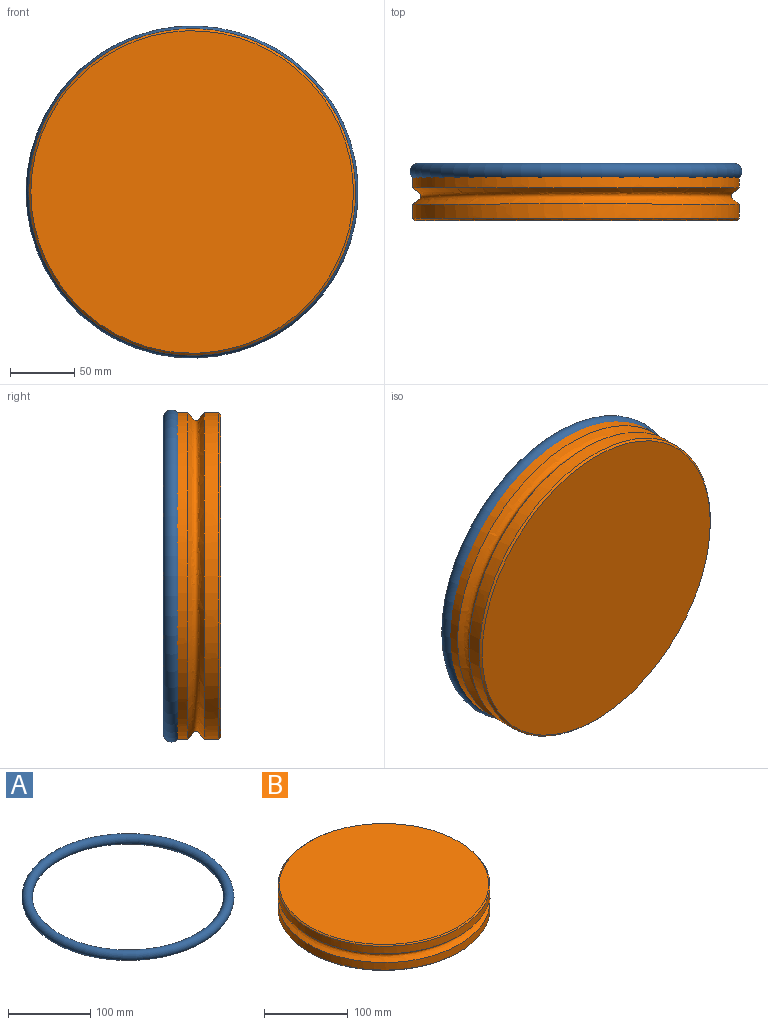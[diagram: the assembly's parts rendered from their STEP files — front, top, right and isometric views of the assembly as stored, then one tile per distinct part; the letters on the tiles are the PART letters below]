
ASSEMBLY  parts=2 mates=1
PART A: 1 faces, bbox 279.6x279.6x12.7 mm
  f0: torus R=122.8mm, axis (0,0,-1), area 30855.3mm2
PART B: 7 faces, bbox 254.1x254.1x38.2 mm
  f0: bspline ~254x254mm, area 14347.4mm2, adj f1,f3
  f1: extruded ~254x254mm, area 8867.4mm2, adj f0,f6
  f2: plane 250.94x250.93mm, normal (0,0,1), area 49405.8mm2, adj f6
  f3: extruded ~254x254mm, area 8867.4mm2, adj f0,f5
  f4: plane 250.94x250.93mm, normal (0,0,-1), area 49405.8mm2, adj f5
  f5: bspline ~254x254mm, area 1780.2mm2, adj f3,f4
  f6: bspline ~254x254mm, area 1780.2mm2, adj f1,f2
PLACE A rot(axis=(-1,0,0),90deg) t=(0,0,0)mm
PLACE B rot(axis=(0,0.71,0.71),180deg) t=(0,-25.4,0)mm
MATE fastened A.f0 <-> B.f2  axis (0,-1,0) through (0,0,0)mm
